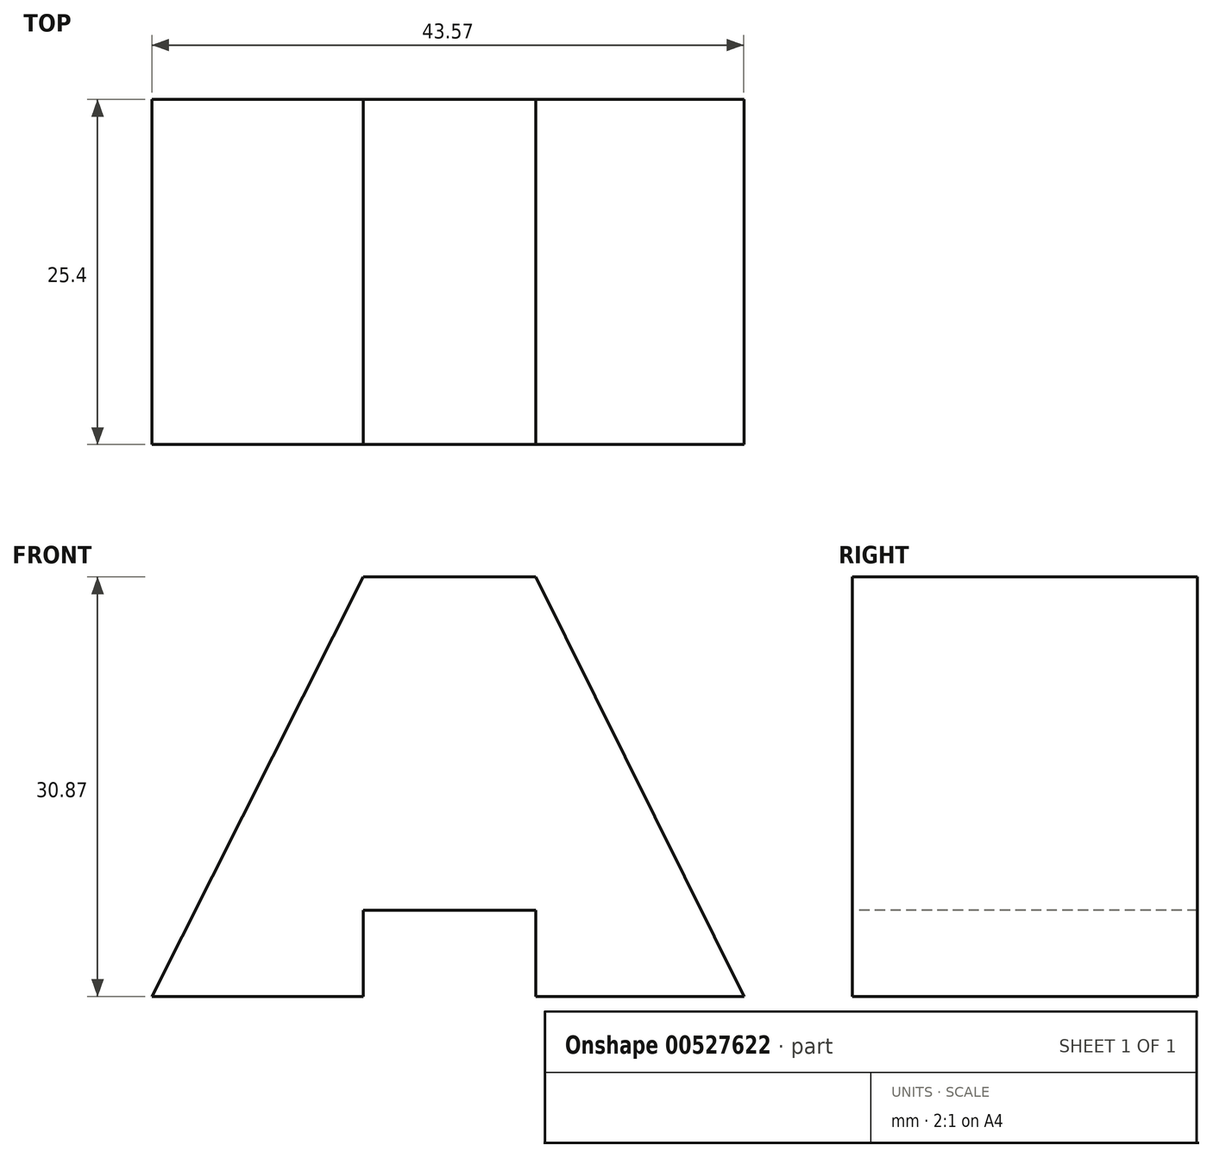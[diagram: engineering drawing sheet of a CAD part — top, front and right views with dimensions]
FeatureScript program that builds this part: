
annotation { "Feature Type Name" : "Feature", "Feature Type Description" : "" }
export const myFeature = defineFeature(function(context is Context, id is Id, definition is map)
    precondition{}
    {
        {
            var Q0;
            Q0=qCreatedBy(makeId("Front.planeOp"),FACE);
            var sketch = newSketch(context, id + "F0", { "sketchPlane" : qUnion([Q0])});
            skLineSegment(sketch, "E0", {"start": v(0, 0) * mm, "end": v(43.57, 0) * mm});
            skLineSegment(sketch, "E1", {"start": v(43.57, 0) * mm, "end": v(28.25, 30.87) * mm});
            skLineSegment(sketch, "E2", {"start": v(28.25, 30.87) * mm, "end": v(15.55, 30.87) * mm});
            skLineSegment(sketch, "E3", {"start": v(15.55, 30.87) * mm, "end": v(0, 0) * mm});
            skSolve(sketch);
        }
        {
            var Q0;
            Q0=makeQuery(id+"F0.imprint","IMPRINT",FACE,{"disambiguationData":[TD([[makeQuery(id+"F0.imprint","IMPRINT",EDGE,{"derivedFrom":sQuery(id+"F0.wireOp",EDGE,"E0")}),1.0]])]});
            extrude(context, id + "F1", {"entities" : qUnion([Q0]), "depth" : 25.4 * mm, "offsetDistance" : 25.4 * mm});
        }
        {
            var Q0;
            Q0=makeQuery(id+"F1.opExtrude","CAP_FACE",FACE,{"disambiguationData":[OSD([sQuery(id+"F0.wireOp",EDGE,"E0"),sQuery(id+"F0.wireOp",EDGE,"E1"),sQuery(id+"F0.wireOp",EDGE,"E2"),sQuery(id+"F0.wireOp",EDGE,"E3")])],"isStart":false});
            var sketch = newSketch(context, id + "F2", { "sketchPlane" : qUnion([Q0])});
            skLineSegment(sketch, "E4", {"start": v(15.55, 0) * mm, "end": v(28.25, 0) * mm});
            skLineSegment(sketch, "E5", {"start": v(28.25, 0) * mm, "end": v(28.25, 6.35) * mm});
            skLineSegment(sketch, "E6", {"start": v(28.25, 6.35) * mm, "end": v(15.55, 6.35) * mm});
            skLineSegment(sketch, "E7", {"start": v(15.55, 6.35) * mm, "end": v(15.55, 0) * mm});
            skSolve(sketch);
        }
        {
            var Q0;
            Q0=makeQuery(id+"F2.imprint","IMPRINT",FACE,{"disambiguationData":[TD([[makeQuery(id+"F2.imprint","IMPRINT",EDGE,{"derivedFrom":sQuery(id+"F2.wireOp",EDGE,"E4")}),1.0]])]});
            extrude(context, id + "F3", {"entities" : qUnion([Q0]), "operationType" : NewBodyOperationType.REMOVE, "oppositeDirection" : true, "depth" : 25.4 * mm, "offsetDistance" : 25.4 * mm});
        }
    });
